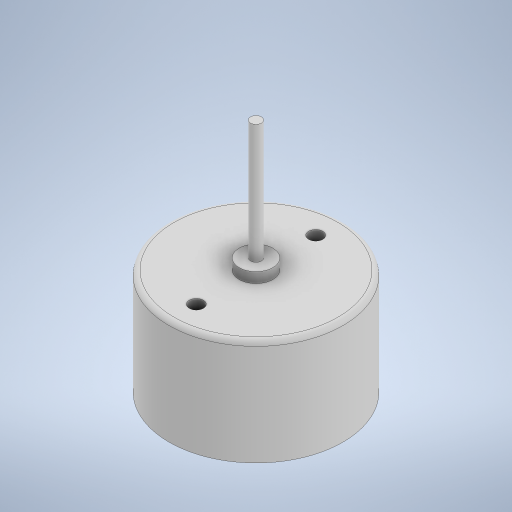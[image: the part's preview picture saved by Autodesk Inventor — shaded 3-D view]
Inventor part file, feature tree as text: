
AUTODESK INVENTOR PART (.ipt)
format: ipt  version: 2024 (Build 280153000, 153)  size: 255,488 bytes
history: native  units: mm
features: extrude x4, sketch x4, projected_geometry x3, fillet x1
ambient origin geometry x8: Origin, YZ Plane, XZ Plane, XY Plane, X Axis, Y Axis, Z Axis, Center Point
bodies: Solid1 (feature_tree)
feature tree (12):
  extrude  "Extrusion1"  Depth=19.5mm TaperAngle=0.0deg
  extrude  "Extrusion2"  Depth=1.9mm TaperAngle=0.0deg
  extrude  "Extrusion3"  Depth=22.0mm TaperAngle=0.0deg
  extrude  "Extrusion4"  Depth=22.0mm
  fillet  "Fillet1"  Radius=4.0mm
  sketch  "Sketch1"  dims[d0=32.0mm d1=19.5mm d2=0.0mm]
  sketch  "Sketch2"  dims[d3=6.2mm d4=1.9mm d5=0.0mm]
  projected_geometry  "Projected Loop1"
  sketch  "Sketch3"  dims[d6=2.0mm d7=22.0mm d8=0.0mm]
  projected_geometry  "Projected Loop2"
  sketch  "Sketch4"  dims[d9=2.6mm d10=22.0mm d11=4.0mm d12=0.0mm d13=0.9mm]
  projected_geometry  "Projected Loop3"
